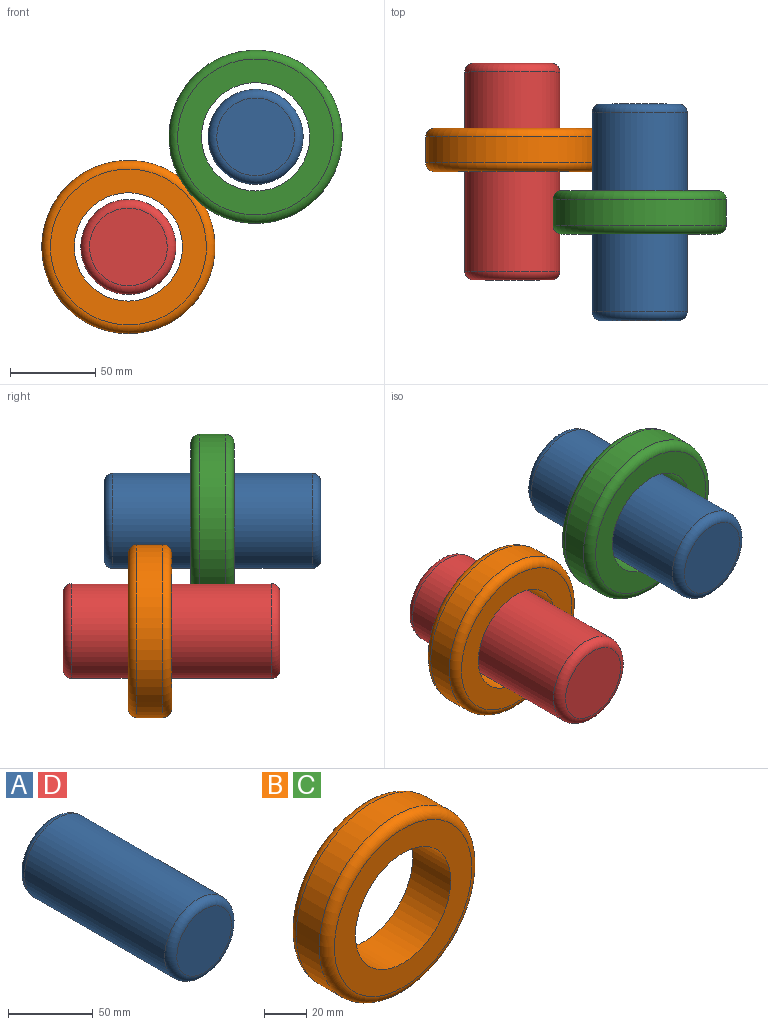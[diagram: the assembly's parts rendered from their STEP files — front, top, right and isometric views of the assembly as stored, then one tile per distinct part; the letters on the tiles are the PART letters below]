
ASSEMBLY  parts=4 mates=1
PART A: 5 faces, bbox 60.3x127x60.3 mm
  f0: cylinder r=27.86mm len=116.84mm, axis (0,-1,0), area 20455.9mm2, adj f3,f4
  f1: plane 45.57x45.57mm, normal (0,1,0), area 1630.9mm2, adj f4
  f2: plane 45.57x45.57mm, normal (0,-1,0), area 1630.9mm2, adj f3
  f3: torus R=22.78mm, axis (0,-1,0), area 1304.5mm2, adj f0,f2
  f4: torus R=22.78mm, axis (0,-1,0), area 1304.5mm2, adj f0,f1
PART B: 6 faces, bbox 110x25.4x110 mm
  f0: cylinder r=31.75mm len=63.5mm, axis (0,-1,0), area 5067.1mm2, adj f2,f3
  f1: cylinder r=50.8mm len=101.6mm, axis (0,-1,0), area 4864.4mm2, adj f4,f5
  f2: plane 91.44x91.44mm, normal (0,1,0), area 3400mm2, adj f0,f5
  f3: plane 91.44x91.44mm, normal (0,-1,0), area 3400mm2, adj f0,f4
  f4: torus R=45.72mm, axis (0,-1,0), area 2454.4mm2, adj f1,f3
  f5: torus R=45.72mm, axis (0,-1,0), area 2454.4mm2, adj f1,f2
PART C: same geometry as B
PART D: same geometry as A
PLACE A rot(axis=(0.21,-0.43,0.88),0deg) t=(36.17,-43.32,68.82)mm
PLACE B t=(-38.44,-19.36,4.25)mm
PLACE C t=(36.17,-56.02,68.82)mm
PLACE D t=(-38.44,-19.36,4.25)mm
MATE slider C.f0 <-> A.f0  axis (0,-1,0) through (36.17,-43.32,68.82)mm
